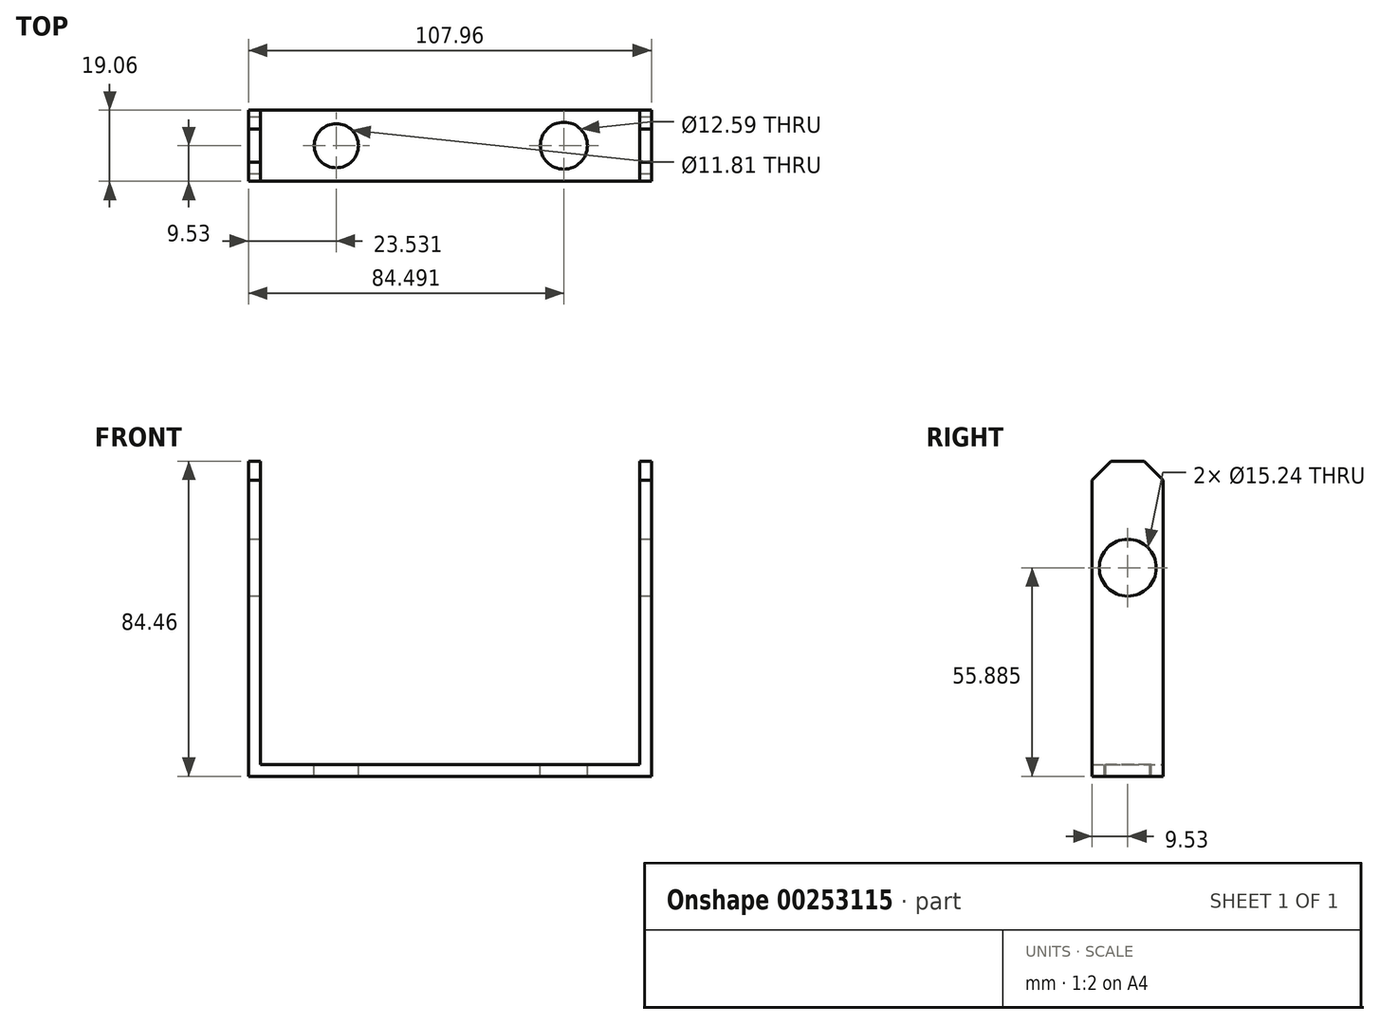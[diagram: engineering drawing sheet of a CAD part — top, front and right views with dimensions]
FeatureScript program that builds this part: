
annotation { "Feature Type Name" : "Feature", "Feature Type Description" : "" }
export const myFeature = defineFeature(function(context is Context, id is Id, definition is map)
    precondition{}
    {
        {
            var Q0;
            Q0=qCreatedBy(makeId("Top.planeOp"),FACE);
            var sketch = newSketch(context, id + "F0", { "sketchPlane" : qUnion([Q0])});
            skLineSegment(sketch, "E0.bottom", {"start": v(53.98, -9.53) * mm, "end": v(-53.98, -9.53) * mm});
            skLineSegment(sketch, "E0.top", {"start": v(53.98, 9.53) * mm, "end": v(-53.98, 9.53) * mm});
            skLineSegment(sketch, "E0.left", {"start": v(53.98, -9.53) * mm, "end": v(53.98, 9.52) * mm});
            skLineSegment(sketch, "E0.right", {"start": v(-53.98, -9.53) * mm, "end": v(-53.98, 9.52) * mm});
            skPoint(sketch, "E0.middle", {"position": v(0, 0) * mm});
            skSolve(sketch);
        }
        {
            var Q0;
            Q0 = qSketchRegion(id + "F0", true);
            extrude(context, id + "F1", {"entities" : qUnion([Q0]), "oppositeDirection" : true, "depth" : 3.17 * mm});
        }
        {
            var Q0;
            Q0=qCreatedBy(makeId("Top.planeOp"),FACE);
            var sketch = newSketch(context, id + "F2", { "sketchPlane" : qUnion([Q0])});
            skLineSegment(sketch, "E1.bottom", {"start": v(-53.98, -9.53) * mm, "end": v(-50.8, -9.53) * mm});
            skLineSegment(sketch, "E1.top", {"start": v(-53.98, 9.52) * mm, "end": v(-50.8, 9.52) * mm});
            skLineSegment(sketch, "E1.left", {"start": v(-53.98, -9.53) * mm, "end": v(-53.98, 9.52) * mm});
            skLineSegment(sketch, "E1.right", {"start": v(-50.8, -9.53) * mm, "end": v(-50.8, 9.52) * mm});
            skLineSegment(sketch, "E2", {"start": v(0, 0) * mm, "end": v(0, 74.7) * mm, "construction": true});
            skLineSegment(sketch, "E3.MirrorCS", {"start": v(50.8, -9.53) * mm, "end": v(50.8, 9.52) * mm});
            skLineSegment(sketch, "E4.MirrorCS", {"start": v(53.98, 9.52) * mm, "end": v(50.8, 9.52) * mm});
            skLineSegment(sketch, "E5.MirrorCS", {"start": v(53.98, -9.53) * mm, "end": v(53.98, 9.52) * mm});
            skLineSegment(sketch, "E6.MirrorCS", {"start": v(53.98, -9.53) * mm, "end": v(50.8, -9.53) * mm});
            skSolve(sketch);
        }
        {
            var Q0;
            Q0 = qSketchRegion(id + "F2", true);
            extrude(context, id + "F3", {"entities" : qUnion([Q0]), "operationType" : NewBodyOperationType.ADD, "depth" : 81.28 * mm});
        }
        {
            var Q0;
            Q0=makeQuery(id+"F3.opExtrude","CAP_EDGE",EDGE,{"disambiguationData":[OSD([sQuery(id+"F2.wireOp",EDGE,"E6.MirrorCS")])],"isStart":false});
            var Q1;
            Q1=makeQuery(id+"F3.opExtrude","CAP_EDGE",EDGE,{"disambiguationData":[OSD([sQuery(id+"F2.wireOp",EDGE,"E4.MirrorCS")])],"isStart":false});
            var Q2;
            Q2=makeQuery(id+"F3.opExtrude","CAP_EDGE",EDGE,{"disambiguationData":[OSD([sQuery(id+"F2.wireOp",EDGE,"E1.bottom")])],"isStart":false});
            var Q3;
            Q3=makeQuery(id+"F3.opExtrude","CAP_EDGE",EDGE,{"disambiguationData":[OSD([sQuery(id+"F2.wireOp",EDGE,"E1.top")])],"isStart":false});
            chamfer(context, id + "F4", {"entities" : qUnion([Q0, Q1, Q2, Q3]), "width" : 5.08 * mm, "tangentPropagation" : true});
        }
        {
            var Q0;
            Q0=makeQuery(id+"F3.boolean.opBoolean","MERGE",FACE,{"derivedFrom":[makeQuery(id+"F1.opExtrude","SWEPT_FACE",FACE,{"disambiguationData":[OSD([sQuery(id+"F0.wireOp",EDGE,"E0.right")])]}),makeQuery(id+"F3.opExtrude","SWEPT_FACE",FACE,{"disambiguationData":[OSD([sQuery(id+"F2.wireOp",EDGE,"E1.left")])]})]});
            var sketch = newSketch(context, id + "F5", { "sketchPlane" : qUnion([Q0])});
            skCircle(sketch, "E7", {"center": v(0, 52.7) * mm, "radius": 7.62 * mm});
            skSolve(sketch);
        }
        {
            var Q0;
            Q0 = qSketchRegion(id + "F5", true);
            var Q1;
            Q1=makeQuery(id+"F3.boolean.opBoolean","MERGE",FACE,{"derivedFrom":[makeQuery(id+"F1.opExtrude","SWEPT_FACE",FACE,{"disambiguationData":[OSD([sQuery(id+"F0.wireOp",EDGE,"E0.left")])]}),makeQuery(id+"F3.opExtrude","SWEPT_FACE",FACE,{"disambiguationData":[OSD([sQuery(id+"F2.wireOp",EDGE,"E5.MirrorCS")])]})]});
            extrude(context, id + "F6", {"entities" : qUnion([Q0]), "operationType" : NewBodyOperationType.REMOVE, "endBound" : BoundingType.UP_TO_SURFACE, "oppositeDirection" : true, "endBoundEntityFace" : qUnion([Q1]), "depth" : 25.4 * mm});
        }
        {
            var Q0;
            Q0=makeQuery(id+"F1.opExtrude","CAP_FACE",FACE,{"disambiguationData":[OSD([sQuery(id+"F0.wireOp",EDGE,"E0.bottom"),sQuery(id+"F0.wireOp",EDGE,"E0.top"),sQuery(id+"F0.wireOp",EDGE,"E0.left"),sQuery(id+"F0.wireOp",EDGE,"E0.right")])],"isStart":true});
            var sketch = newSketch(context, id + "F7", { "sketchPlane" : qUnion([Q0])});
            skCircle(sketch, "E8", {"center": v(-30.45, 0) * mm, "radius": 5.9 * mm});
            skCircle(sketch, "E9", {"center": v(30.51, 0) * mm, "radius": 6.3 * mm});
            skSolve(sketch);
        }
        {
            var Q0;
            Q0 = qSketchRegion(id + "F7", true);
            var Q1;
            Q1=makeQuery(id+"F1.opExtrude","CAP_FACE",FACE,{"disambiguationData":[OSD([sQuery(id+"F0.wireOp",EDGE,"E0.bottom"),sQuery(id+"F0.wireOp",EDGE,"E0.top"),sQuery(id+"F0.wireOp",EDGE,"E0.left"),sQuery(id+"F0.wireOp",EDGE,"E0.right")])],"isStart":false});
            extrude(context, id + "F8", {"entities" : qUnion([Q0]), "operationType" : NewBodyOperationType.REMOVE, "endBound" : BoundingType.UP_TO_SURFACE, "oppositeDirection" : true, "endBoundEntityFace" : qUnion([Q1]), "depth" : 25.4 * mm});
        }
    });
